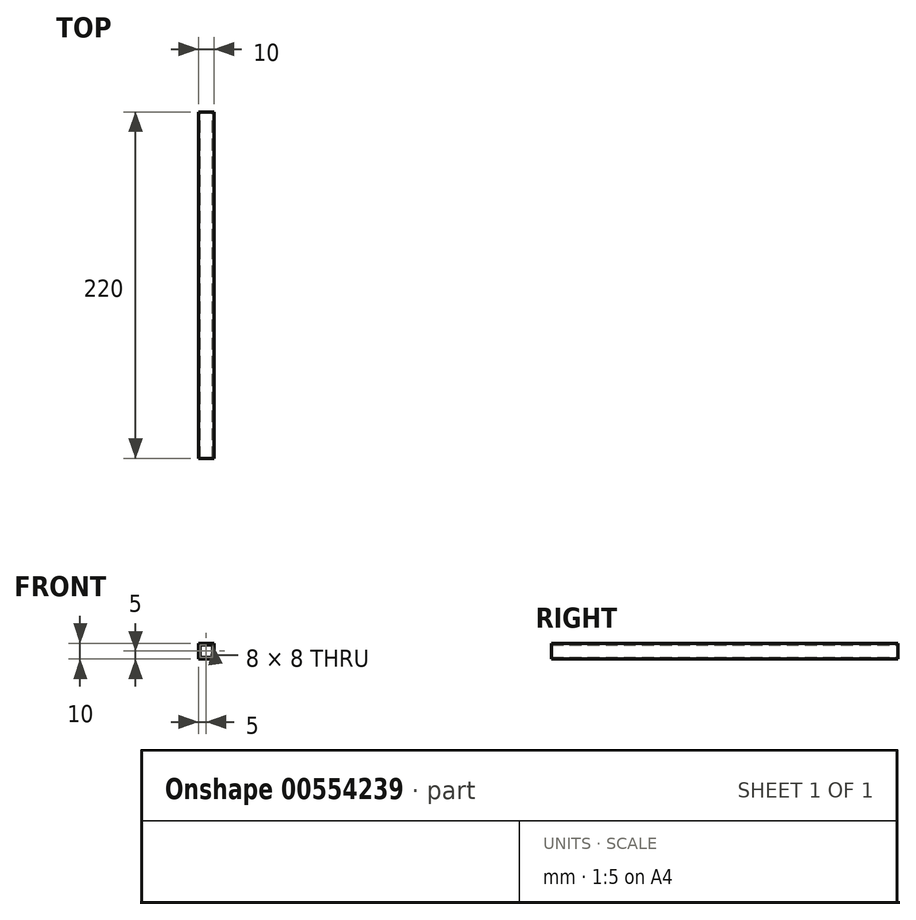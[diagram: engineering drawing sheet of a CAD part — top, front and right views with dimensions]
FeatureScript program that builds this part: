
annotation { "Feature Type Name" : "Feature", "Feature Type Description" : "" }
export const myFeature = defineFeature(function(context is Context, id is Id, definition is map)
    precondition{}
    {
        {
            var Q0;
            Q0=qCreatedBy(makeId("Front.planeOp"),FACE);
            var sketch = newSketch(context, id + "F0", { "sketchPlane" : qUnion([Q0])});
            skLineSegment(sketch, "E0.bottom", {"start": v(-5, 5) * mm, "end": v(5, 5) * mm});
            skLineSegment(sketch, "E0.top", {"start": v(-5, -5) * mm, "end": v(5, -5) * mm});
            skLineSegment(sketch, "E0.left", {"start": v(-5, 5) * mm, "end": v(-5, -5) * mm});
            skLineSegment(sketch, "E0.right", {"start": v(5, 5) * mm, "end": v(5, -5) * mm});
            skPoint(sketch, "E0.middle", {"position": v(0, 0) * mm});
            skLineSegment(sketch, "E1.0", {"start": v(4, 4) * mm, "end": v(4, -4) * mm});
            skLineSegment(sketch, "E1.1", {"start": v(-4, 4) * mm, "end": v(4, 4) * mm});
            skLineSegment(sketch, "E1.2", {"start": v(-4, 4) * mm, "end": v(-4, -4) * mm});
            skLineSegment(sketch, "E1.3", {"start": v(-4, -4) * mm, "end": v(4, -4) * mm});
            skSolve(sketch);
        }
        {
            var Q0;
            Q0=makeQuery(id+"F0.imprint","IMPRINT",FACE,{"disambiguationData":[TD([[makeQuery(id+"F0.imprint","IMPRINT",EDGE,{"derivedFrom":sQuery(id+"F0.wireOp",EDGE,"E0.bottom")}),-1.0]])]});
            extrude(context, id + "F1", {"entities" : qUnion([Q0]), "depth" : 220 * mm, "offsetDistance" : 25 * mm});
        }
    });
